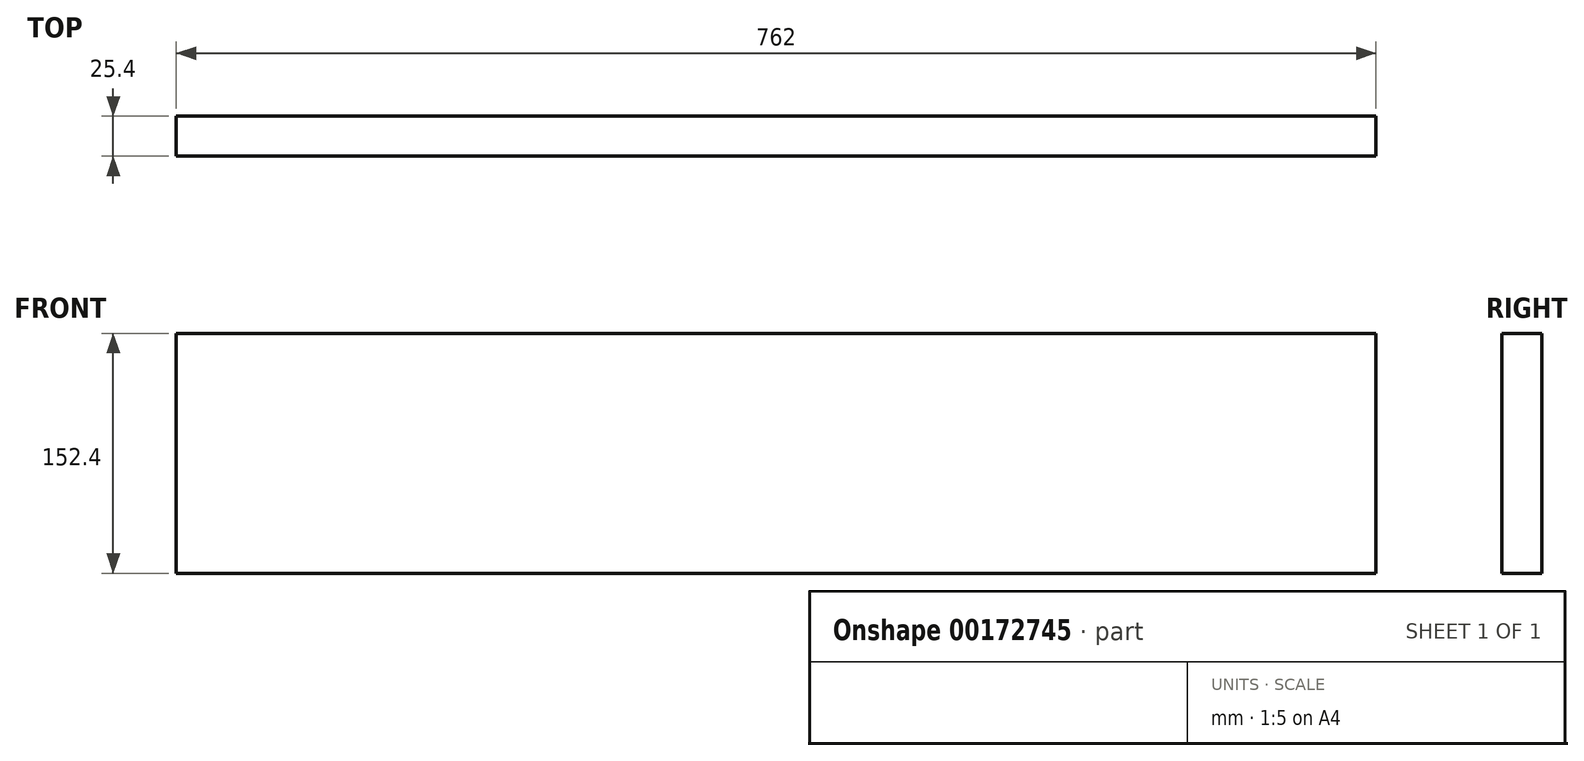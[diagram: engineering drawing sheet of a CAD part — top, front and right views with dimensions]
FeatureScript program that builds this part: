
annotation { "Feature Type Name" : "Feature", "Feature Type Description" : "" }
export const myFeature = defineFeature(function(context is Context, id is Id, definition is map)
    precondition{}
    {
        {
            var Q0;
            Q0=qCreatedBy(makeId("Front.planeOp"),FACE);
            var sketch = newSketch(context, id + "F0", { "sketchPlane" : qUnion([Q0])});
            skLineSegment(sketch, "E0.bottom", {"start": v(-387.63, 74.33) * mm, "end": v(374.37, 74.33) * mm});
            skLineSegment(sketch, "E0.top", {"start": v(-387.63, -78.07) * mm, "end": v(374.37, -78.07) * mm});
            skLineSegment(sketch, "E0.left", {"start": v(-387.63, 74.33) * mm, "end": v(-387.63, -78.07) * mm});
            skLineSegment(sketch, "E0.right", {"start": v(374.37, 74.33) * mm, "end": v(374.37, -78.07) * mm});
            skSolve(sketch);
        }
        {
            var Q0;
            Q0 = qSketchRegion(id + "F0", true);
            extrude(context, id + "F1", {"entities" : qUnion([Q0]), "depth" : 25.4 * mm});
        }
    });
